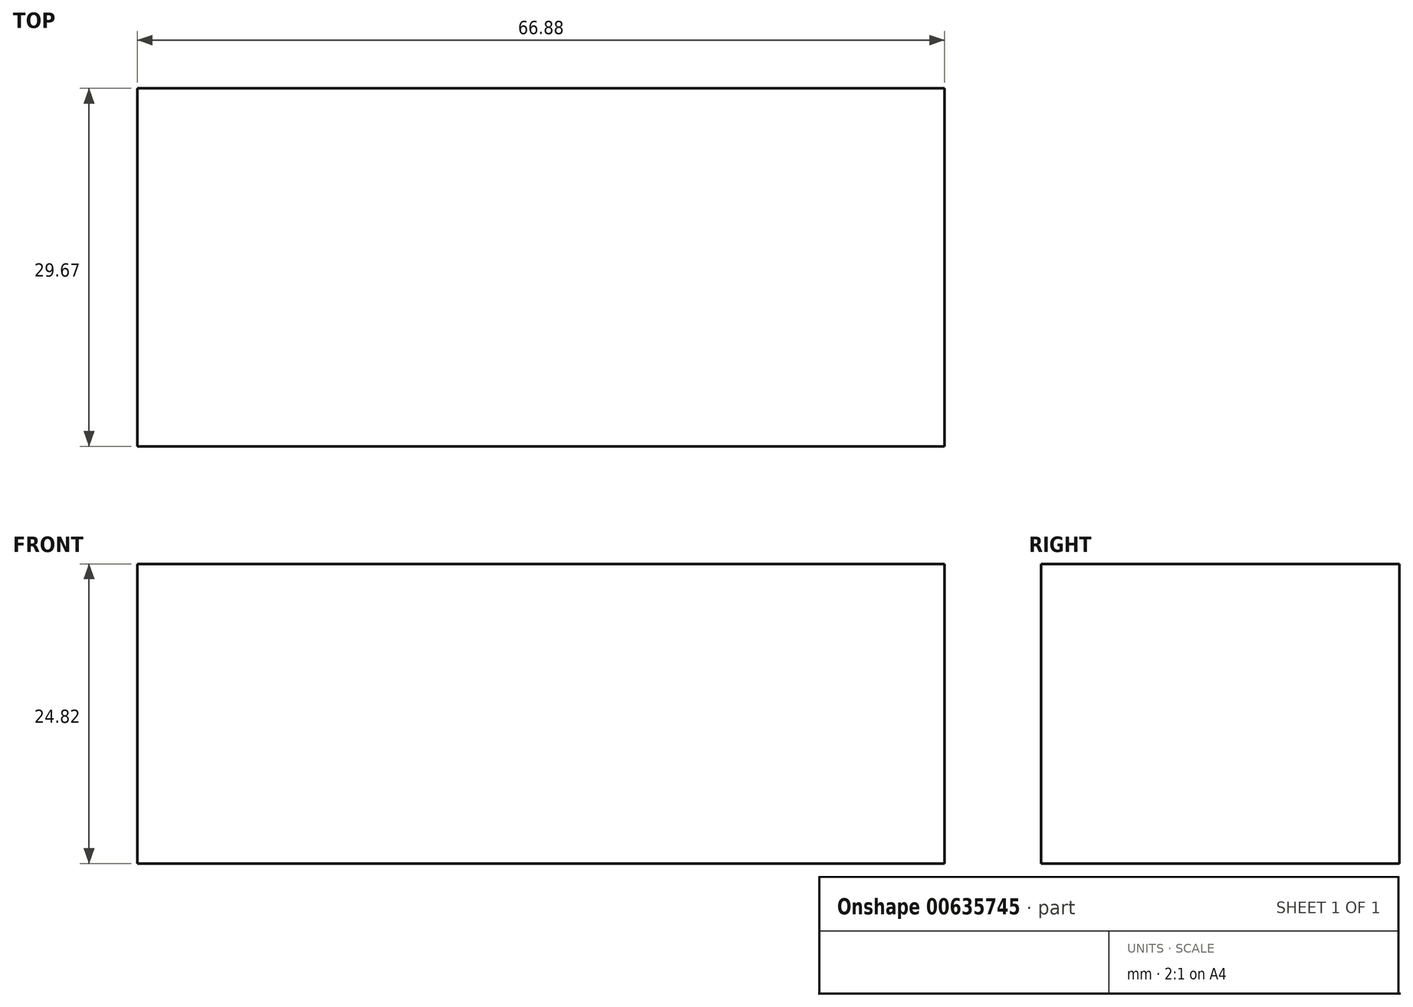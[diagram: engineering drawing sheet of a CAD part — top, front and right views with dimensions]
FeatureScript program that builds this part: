
annotation { "Feature Type Name" : "Feature", "Feature Type Description" : "" }
export const myFeature = defineFeature(function(context is Context, id is Id, definition is map)
    precondition{}
    {
        {
            var Q0;
            Q0=qCreatedBy(makeId("Front.planeOp"),FACE);
            var sketch = newSketch(context, id + "F0", { "sketchPlane" : qUnion([Q0])});
            skLineSegment(sketch, "E0", {"start": v(-44.06, 43.28) * mm, "end": v(-44.06, 18.46) * mm});
            skLineSegment(sketch, "E1", {"start": v(-44.06, 18.46) * mm, "end": v(22.82, 18.46) * mm});
            skLineSegment(sketch, "E2", {"start": v(22.82, 18.46) * mm, "end": v(22.82, 43.28) * mm});
            skLineSegment(sketch, "E3", {"start": v(22.82, 43.28) * mm, "end": v(-44.06, 43.28) * mm});
            skSolve(sketch);
        }
        {
            var Q0;
            Q0=makeQuery(id+"F0.imprint","IMPRINT",FACE,{"disambiguationData":[TD([[makeQuery(id+"F0.imprint","IMPRINT",EDGE,{"derivedFrom":sQuery(id+"F0.wireOp",EDGE,"E0")}),1.0]])]});
            extrude(context, id + "F1", {"entities" : qUnion([Q0]), "depth" : 29.67 * mm, "offsetDistance" : 25.4 * mm});
        }
    });
